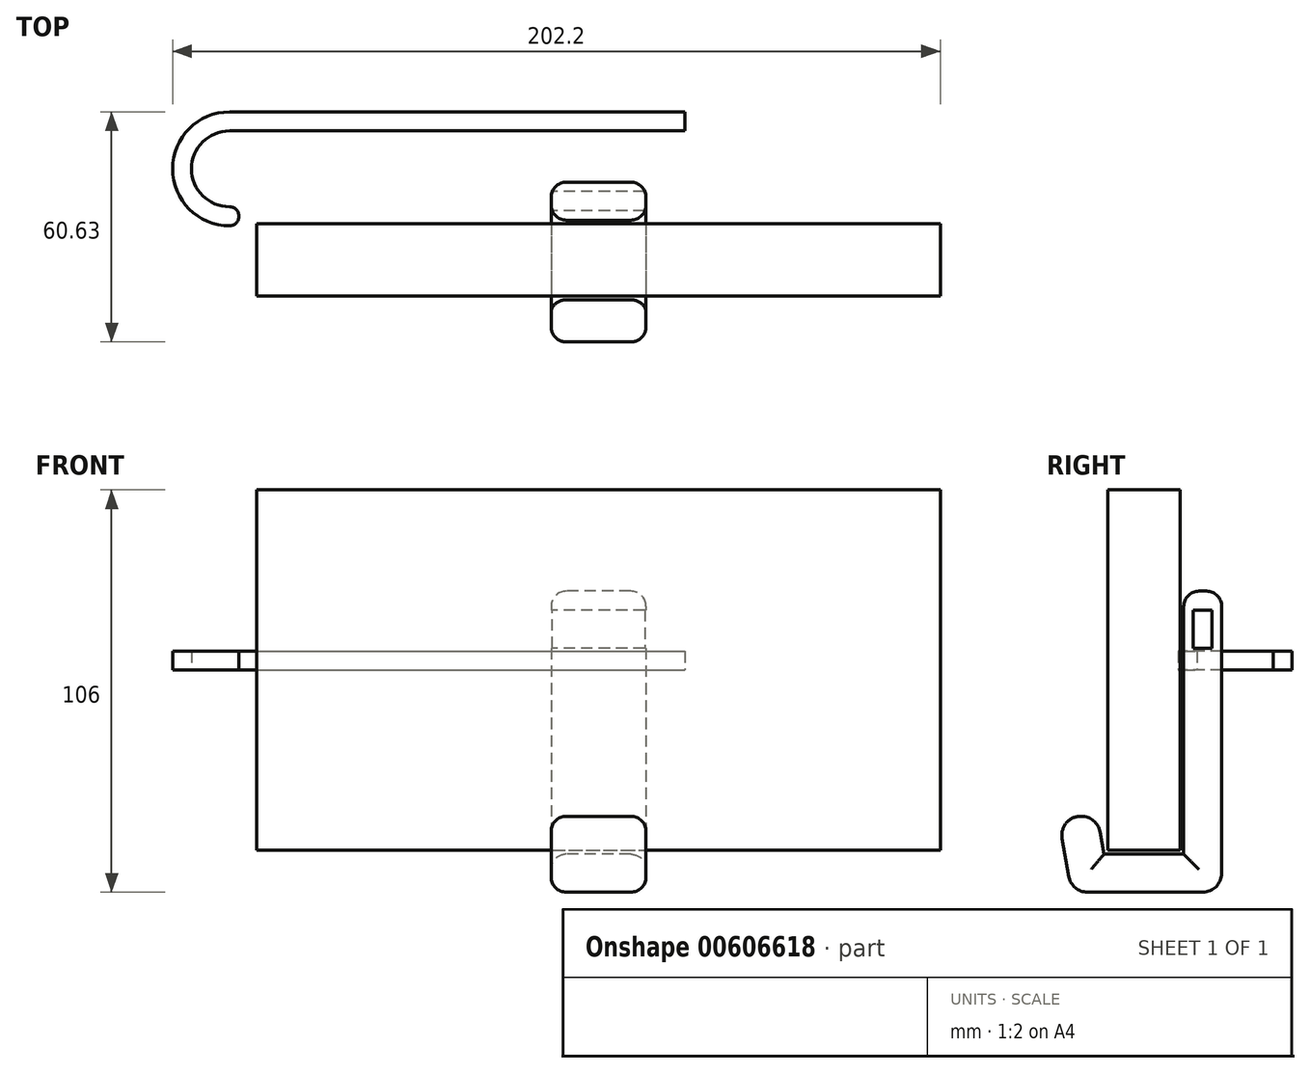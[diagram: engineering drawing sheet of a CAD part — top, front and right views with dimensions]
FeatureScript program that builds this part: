
annotation { "Feature Type Name" : "Feature", "Feature Type Description" : "" }
export const myFeature = defineFeature(function(context is Context, id is Id, definition is map)
    precondition{}
    {
        {
            var Q0;
            Q0=qCreatedBy(makeId("Front.planeOp"),FACE);
            var sketch = newSketch(context, id + "F0", { "sketchPlane" : qUnion([Q0])});
            skLineSegment(sketch, "E0.bottom", {"start": v(-90, 47.5) * mm, "end": v(90, 47.5) * mm});
            skLineSegment(sketch, "E0.top", {"start": v(-90, -47.5) * mm, "end": v(90, -47.5) * mm});
            skLineSegment(sketch, "E0.left", {"start": v(-90, 47.5) * mm, "end": v(-90, -47.5) * mm});
            skLineSegment(sketch, "E0.right", {"start": v(90, 47.5) * mm, "end": v(90, -47.5) * mm});
            skSolve(sketch);
        }
        {
            var Q0;
            Q0 = qSketchRegion(id + "F0", true);
            extrude(context, id + "F1", {"entities" : qUnion([Q0]), "endBound" : BoundingType.SYMMETRIC, "depth" : 19 * mm, "offsetDistance" : 25 * mm});
        }
        {
            var Q0;
            Q0=makeQuery(id+"F1.opExtrude","CAP_FACE",FACE,{"disambiguationData":[OSD([sQuery(id+"F0.wireOp",EDGE,"E0.bottom"),sQuery(id+"F0.wireOp",EDGE,"E0.top"),sQuery(id+"F0.wireOp",EDGE,"E0.left"),sQuery(id+"F0.wireOp",EDGE,"E0.right")])],"isStart":true});
            var sketch = newSketch(context, id + "F2", { "sketchPlane" : qUnion([Q0])});
            skLineSegment(sketch, "E1", {"start": v(0, 47.5) * mm, "end": v(0, 15.83) * mm, "construction": true});
            skLineSegment(sketch, "E2", {"start": v(0, 15.83) * mm, "end": v(0, -15.83) * mm, "construction": true});
            skLineSegment(sketch, "E3", {"start": v(0, -15.83) * mm, "end": v(0, -47.5) * mm, "construction": true});
            skSolve(sketch);
        }
        {
            var Q0;
            Q0=qCreatedBy(makeId("Right.planeOp"),FACE);
            var sketch = newSketch(context, id + "F3", { "sketchPlane" : qUnion([Q0])});
            skLineSegment(sketch, "E4.bottom", {"start": v(20.5, 20.83) * mm, "end": v(10.5, 20.83) * mm});
            skLineSegment(sketch, "E4.top", {"start": v(20.5, -48.5) * mm, "end": v(10.5, -48.5) * mm});
            skLineSegment(sketch, "E4.left", {"start": v(20.5, 20.83) * mm, "end": v(20.5, -48.5) * mm});
            skLineSegment(sketch, "E4.right", {"start": v(10.5, 20.83) * mm, "end": v(10.5, -48.5) * mm});
            skLineSegment(sketch, "E5.bottom", {"start": v(20.5, -48.5) * mm, "end": v(-10.5, -48.5) * mm});
            skLineSegment(sketch, "E5.top", {"start": v(15.5, -58.5) * mm, "end": v(-10.5, -58.5) * mm});
            skLineSegment(sketch, "E5.left", {"start": v(20.5, -48.5) * mm, "end": v(20.5, -53.5) * mm});
            skLineSegment(sketch, "E5.right", {"start": v(-10.5, -48.5) * mm, "end": v(-10.5, -58.5) * mm});
            skLineSegment(sketch, "E6.bottom", {"start": v(-8.74, -58.5) * mm, "end": v(-14.85, -58.5) * mm});
            skLineSegment(sketch, "E6.top", {"start": v(-16.46, -38.5) * mm, "end": v(-16.61, -38.5) * mm});
            skLineSegment(sketch, "E6.left", {"start": v(-8.74, -58.5) * mm, "end": v(-11.53, -42.63) * mm});
            skLineSegment(sketch, "E6.right", {"start": v(-19.77, -54.37) * mm, "end": v(-21.53, -44.37) * mm});
            skLineSegment(sketch, "E7.bottom", {"start": v(18, 15.83) * mm, "end": v(13, 15.83) * mm});
            skLineSegment(sketch, "E7.top", {"start": v(18, 5.83) * mm, "end": v(13, 5.83) * mm});
            skLineSegment(sketch, "E7.left", {"start": v(18, 15.83) * mm, "end": v(18, 5.83) * mm});
            skLineSegment(sketch, "E7.right", {"start": v(13, 15.83) * mm, "end": v(13, 5.83) * mm});
            skPoint(sketch, "E8.visualSharp", {"position": v(20.5, -58.5) * mm});
            skArc(sketch, "E8.filletArc", {"start": v(15.5, -58.5) * mm, "mid": v(19.04, -57.04) * mm, "end": v(20.5, -53.5) * mm});
            skPoint(sketch, "E9.visualSharp", {"position": v(-19.04, -58.5) * mm});
            skArc(sketch, "E9.filletArc", {"start": v(-19.77, -54.37) * mm, "mid": v(-18.06, -57.33) * mm, "end": v(-14.85, -58.5) * mm});
            skPoint(sketch, "E10.visualSharp", {"position": v(-12.26, -38.5) * mm});
            skArc(sketch, "E10.filletArc", {"start": v(-11.53, -42.63) * mm, "mid": v(-13.24, -39.67) * mm, "end": v(-16.46, -38.5) * mm});
            skPoint(sketch, "E11.visualSharp", {"position": v(-22.57, -38.5) * mm});
            skArc(sketch, "E11.filletArc", {"start": v(-16.61, -38.5) * mm, "mid": v(-20.44, -40.29) * mm, "end": v(-21.53, -44.37) * mm});
            skLineSegment(sketch, "E12", {"start": v(13, 5.83) * mm, "end": v(20.5, 20.83) * mm, "construction": true});
            skLineSegment(sketch, "E13", {"start": v(18, 5.83) * mm, "end": v(10.5, 20.83) * mm, "construction": true});
            skSolve(sketch);
        }
        {
            var Q0;
            Q0 = qSketchRegion(id + "F3", true);
            extrude(context, id + "F4", {"entities" : qUnion([Q0]), "endBound" : BoundingType.SYMMETRIC, "depth" : 25 * mm, "offsetDistance" : 25 * mm});
        }
        {
            var Q0;
            Q0=makeQuery(id+"F4.opExtrude","CAP_EDGE",EDGE,{"disambiguationData":[OSD([sQuery(id+"F3.wireOp",EDGE,"E6.right")])],"isStart":true});
            var Q1;
            Q1=makeQuery(id+"F4.opExtrude","CAP_EDGE",EDGE,{"disambiguationData":[OSD([sQuery(id+"F3.wireOp",EDGE,"E6.right")])],"isStart":false});
            var Q2;
            Q2=makeQuery(id+"F4.opExtrude","CAP_EDGE",EDGE,{"disambiguationData":[OSD([sQuery(id+"F3.wireOp",EDGE,"E5.bottom")])],"isStart":false});
            var Q3;
            Q3=makeQuery(id+"F4.opExtrude","CAP_EDGE",EDGE,{"disambiguationData":[OSD([sQuery(id+"F3.wireOp",EDGE,"E4.right")])],"isStart":false});
            var Q4;
            Q4=makeQuery(id+"F4.opExtrude","CAP_EDGE",EDGE,{"disambiguationData":[OSD([sQuery(id+"F3.wireOp",EDGE,"E5.bottom")])],"isStart":true});
            var Q5;
            Q5=makeQuery(id+"F4.opExtrude","CAP_EDGE",EDGE,{"disambiguationData":[OSD([sQuery(id+"F3.wireOp",EDGE,"E4.right")])],"isStart":true});
            var Q6;
            Q6=makeQuery(id+"F4.opExtrude","SWEPT_FACE",FACE,{"disambiguationData":[OSD([sQuery(id+"F3.wireOp",EDGE,"E4.bottom")])]});
            fillet(context, id + "F5", {"entities" : qUnion([Q0, Q1, Q2, Q3, Q4, Q5, Q6]), "radius" : 4 * mm, "tangentPropagation" : true, "allowEdgeOverflow" : false});
        }
        {
            var Q0;
            Q0=qCreatedBy(makeId("Top.planeOp"),FACE);
            var sketch = newSketch(context, id + "F6", { "sketchPlane" : qUnion([Q0])});
            skLineSegment(sketch, "E14.bottom", {"start": v(-97.2, 39.02) * mm, "end": v(22.7, 39.02) * mm});
            skLineSegment(sketch, "E14.top", {"start": v(-97.2, 34.02) * mm, "end": v(22.7, 34.02) * mm});
            skLineSegment(sketch, "E14.left", {"start": v(-97.2, 39.02) * mm, "end": v(-97.2, 34.02) * mm});
            skLineSegment(sketch, "E14.right", {"start": v(22.7, 39.02) * mm, "end": v(22.7, 34.02) * mm});
            skArc(sketch, "E15", {"start": v(-97.2, 34.02) * mm, "mid": v(-107.2, 24.02) * mm, "end": v(-97.2, 14.02) * mm});
            skArc(sketch, "E16", {"start": v(-97.2, 39.02) * mm, "mid": v(-112.2, 24.02) * mm, "end": v(-97.2, 9.02) * mm});
            skArc(sketch, "E17", {"start": v(-97.2, 9.02) * mm, "mid": v(-94.7, 11.52) * mm, "end": v(-97.2, 14.02) * mm});
            skSolve(sketch);
        }
        {
            var Q0;
            Q0 = qSketchRegion(id + "F6", true);
            extrude(context, id + "F7", {"entities" : qUnion([Q0]), "depth" : 5 * mm, "offsetDistance" : 25 * mm});
        }
    });
